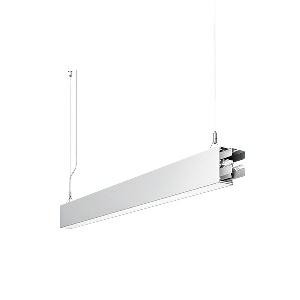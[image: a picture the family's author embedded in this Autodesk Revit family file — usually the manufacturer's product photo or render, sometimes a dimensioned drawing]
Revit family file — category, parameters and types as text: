
# Revit family: idoo_line_-_ilp_3000_vtl_d_sta_00806449_d5c8
name_source: partatom
category: Lighting Fixtures
units: mm (PartAtom-declared; Revit-internal decimal feet)

## family parameters
Cut with Voids When Loaded = No
Host = Face
Light Source = No
Part Type = Normal
Room Calculation Point = No
Round Connector Dimension = Use Diameter
Shared = No

## types (1)
- IDOO.line - ILP 3000/VTL/D STA (1 x LED, 3150 lm, 2700-6500K)
    Apparent Load = 32 VA
    Approval mark = CE
    CIE Flux Codes = 66 91 98 40 100
    Color Rendering = 90-100
    Color Temperature = 2700-6500K
    Control Gear = Electronic ballast
    Default Elevation = 1800 mm
    Description = ILP 3000/VTL/D|Suspended luminaire|light source: LED|connected load: 220-240 V, 50/60 Hz|Power consumption: approx. 32 W|standby: approx. 0,25|luminous flux: 3150 lm|luminous efficacy: 98 lm/W|light distribution: Direct/indirect|direct ratio: approx. 40 %|colour temperature: Cold white, ca. 2700-6500 K|color rendering index (CRI): >= 90|chromaticity tolerance:  3 SDCM|System of protection: IP 40|technology: Continuously dimmable|luminaire body|material: Sectional aluminium|colour: White|lamp cover: Acrylic (PMMA), Clear|mains lead: 2.00 m With free stranded wires|Fastening: Steel cable 0.3 - 0.7 m|glare control: Prism aperture|luminance(L65): <= 2700 cd/m|unified glare rating(4H 8H): <=  16|special features: Specified values at approx. 4000 K, DALI Load 1x, Through-wired, up to 18 m on one mains connection, External control required for Dali Device type 8, Flicker-free, Constant luminous flux between 2700 and 6500 K, Constant colour temperature over the whole dimming range, Suitable as emergency lighting, Start luminaire with mains connection, Mechanical and electrical connection of the individual modules without tools|
    Frequency = 50 Hz
    Height = 110 mm
    Lamp = 1 x LED
    Lamp Light Flux = 3150 lm
    Lamp count = 1
    Length = 1128 mm
    Luminous efficacy = 98 lm/W
    Manufacturer = Waldmann
    ModVariant = No
    Model = 00806449
    Mounting Place = Ceiling
    Mounting Type = Pendant
    Number of Poles = 1
    OnlyDefault = Yes
    Power Factor = 1
    Product Name = IDOO.line - ILP 3000/VTL/D STA
    Product group = Suspended luminaire
    ProductGroupID = 9
    Protection Class = Protection class I
    Protection Degree = IP 40
    RLX_Detail_Level = 1
    RLX_Emergency_Light_Flux = 0 lm
    RLX_Emergency_Type = 0
    RLX_Emergency_Type_DB = No
    RlxData = <blob elided: 21185 chars, md5=38e54ecb>
    Socket = socket
    Standby Power = 0 W
    System Light Flux = 3150 lm
    System Power = 32 W
    Type Comments = Product without accessories
    Type Image = 113301000-00692567.jpg
    URL = http://relux.com
    VarID = ---
    Voltage = 230 V
    Voltage Range = 220-240 V
    Weight = 0.00 kg
    Width = 60 mm  [stored 0.19685 ft]

note: [stored X ft] marks values corroborated as IEEE doubles in the binary element streams (Revit-internal decimal feet)

## geometry (parser evidence)
native form markers: Blend x4, Sweep x14
no freeform markers — native parametric forms only
